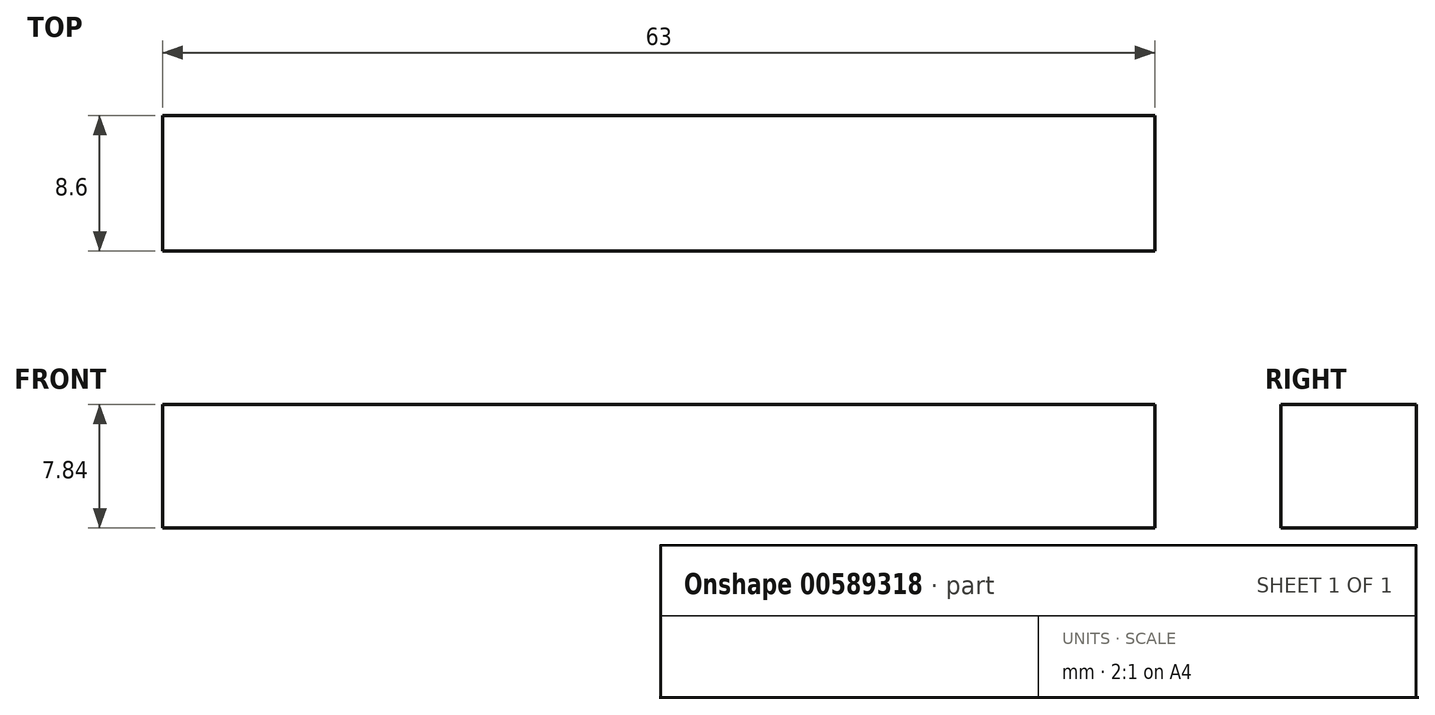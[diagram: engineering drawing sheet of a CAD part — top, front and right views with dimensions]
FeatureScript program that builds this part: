
annotation { "Feature Type Name" : "Feature", "Feature Type Description" : "" }
export const myFeature = defineFeature(function(context is Context, id is Id, definition is map)
    precondition{}
    {
        {
            var Q0;
            Q0=qCreatedBy(makeId("Front.planeOp"),FACE);
            var sketch = newSketch(context, id + "F0", { "sketchPlane" : qUnion([Q0])});
            skLineSegment(sketch, "E0.bottom", {"start": v(-31.5, 3.93) * mm, "end": v(31.5, 3.93) * mm});
            skLineSegment(sketch, "E0.top", {"start": v(-31.5, -3.93) * mm, "end": v(31.5, -3.93) * mm});
            skLineSegment(sketch, "E0.left", {"start": v(-31.5, 3.93) * mm, "end": v(-31.5, -3.93) * mm});
            skLineSegment(sketch, "E0.right", {"start": v(31.5, 3.93) * mm, "end": v(31.5, -3.93) * mm});
            skPoint(sketch, "E0.middle", {"position": v(0, 0) * mm});
            skSolve(sketch);
        }
        {
            var Q0;
            Q0=makeQuery(id+"F0.imprint","IMPRINT",FACE,{"disambiguationData":[TD([[makeQuery(id+"F0.imprint","IMPRINT",EDGE,{"derivedFrom":sQuery(id+"F0.wireOp",EDGE,"E0.bottom")}),-1.0]])]});
            extrude(context, id + "F1", {"entities" : qUnion([Q0]), "depth" : 8.6 * mm, "offsetDistance" : 25.4 * mm});
        }
    });
